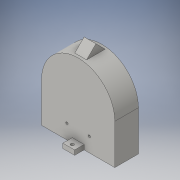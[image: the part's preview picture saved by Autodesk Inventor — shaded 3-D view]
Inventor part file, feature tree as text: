
AUTODESK INVENTOR PART (.ipt)
format: ipt  version: 2016 (Build 200138000, 138)  size: 164,864 bytes
history: native  units: in
note: dims shown in document units (in); Inventor stores cm internally (conversion verified against a paired STEP export)
features: extrude x7, sketch x6, reference x6, plane x1
ambient origin geometry x8: Origin, YZ Plane, XZ Plane, XY Plane, X Axis, Y Axis, Z Axis, Center Point
bodies: Solid1 (feature_tree)
feature tree (20):
  extrude  "Extrusion1"  Depth=3.1in
  extrude  "Extrusion2"  Depth=0.4in TaperAngle=0.0deg
  extrude  "Extrusion4"  Depth=0.1065in
  plane  "Work Plane1"
  extrude  "Extrusion8"  Depth=0.394in
  extrude  "Extrusion10"  Depth=0.5in TaperAngle=0.0deg
  extrude  "Extrusion11"  Depth=0.5in
  extrude  "Extrusion12"  Depth=0.5in
  sketch  "Sketch1"  dims[d1=1.0in d2=0.0in d3=3.1in]
  reference  "Reference1"
  reference  "Reference2"
  reference  "Reference3"
  sketch  "Sketch2"  dims[d5=0.4in d6=0.0in d13=0.4in d14=0.0in]
  reference  "Reference4"
  sketch  "Sketch9"  dims[d29=-1.55in d30=0.1065in]
  sketch  "Sketch11"  dims[d31=0.787in d32=0.394in]
  sketch  "Sketch12"  dims[d33=0.394in d34=0.5in d35=0.0in]
  reference  "Reference12"
  reference  "Reference13"
  sketch  "Sketch13"  dims[d44=0.197in d45=0.25in d46=0.5in d47=0.15in d48=0.177in d49=1.0in d50=0.0in d51=0.0984in d52=0.0984in d53=1.0in d54=0.0in d56=0.25in d57=0.5in d58=0.15in d59=0.138in d60=1.0in d61=0.0in d62=0.5in d63=0.5in]
